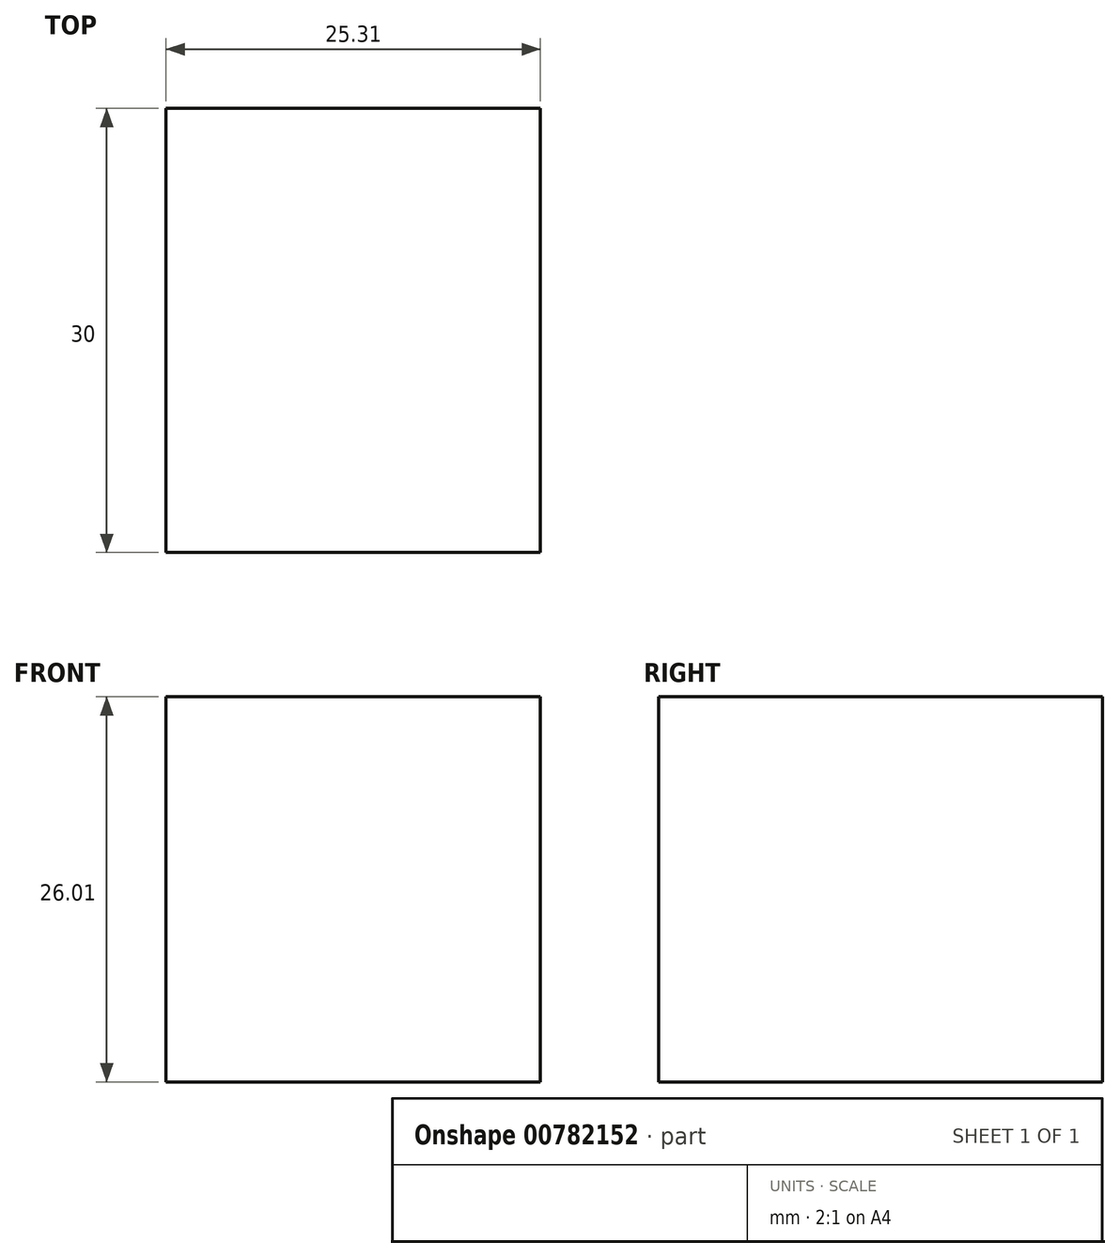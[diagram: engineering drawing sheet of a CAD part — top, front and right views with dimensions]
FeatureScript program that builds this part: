
annotation { "Feature Type Name" : "Feature", "Feature Type Description" : "" }
export const myFeature = defineFeature(function(context is Context, id is Id, definition is map)
    precondition{}
    {
        {
            var Q0;
            Q0=qCreatedBy(makeId("Front.planeOp"),FACE);
            var sketch = newSketch(context, id + "F0", { "sketchPlane" : qUnion([Q0])});
            skLineSegment(sketch, "E0.bottom", {"start": v(0, 0) * mm, "end": v(0, 0) * mm});
            skLineSegment(sketch, "E0.top", {"start": v(0, 0) * mm, "end": v(0, 0) * mm});
            skLineSegment(sketch, "E0.left", {"start": v(0, 0) * mm, "end": v(0, 0) * mm});
            skLineSegment(sketch, "E0.right", {"start": v(0, 0) * mm, "end": v(0, 0) * mm});
            skPoint(sketch, "E0.middle", {"position": v(0, 0) * mm});
            skLineSegment(sketch, "E1.bottom", {"start": v(0, 0) * mm, "end": v(25.31, 0) * mm});
            skLineSegment(sketch, "E1.top", {"start": v(0, 26.01) * mm, "end": v(25.31, 26.01) * mm});
            skLineSegment(sketch, "E1.left", {"start": v(0, 0) * mm, "end": v(0, 26.01) * mm});
            skLineSegment(sketch, "E1.right", {"start": v(25.31, 0) * mm, "end": v(25.31, 26.01) * mm});
            skPoint(sketch, "E1.middle", {"position": v(12.66, 13) * mm});
            skSolve(sketch);
        }
        {
            var Q0;
            Q0=makeQuery(id+"F0.imprint","IMPRINT",FACE,{"disambiguationData":[TD([[makeQuery(id+"F0.imprint","IMPRINT",EDGE,{"derivedFrom":sQuery(id+"F0.wireOp",EDGE,"E1.bottom")}),1.0]])]});
            extrude(context, id + "F1", {"entities" : qUnion([Q0]), "depth" : 30 * mm, "offsetDistance" : 25.4 * mm});
        }
    });
